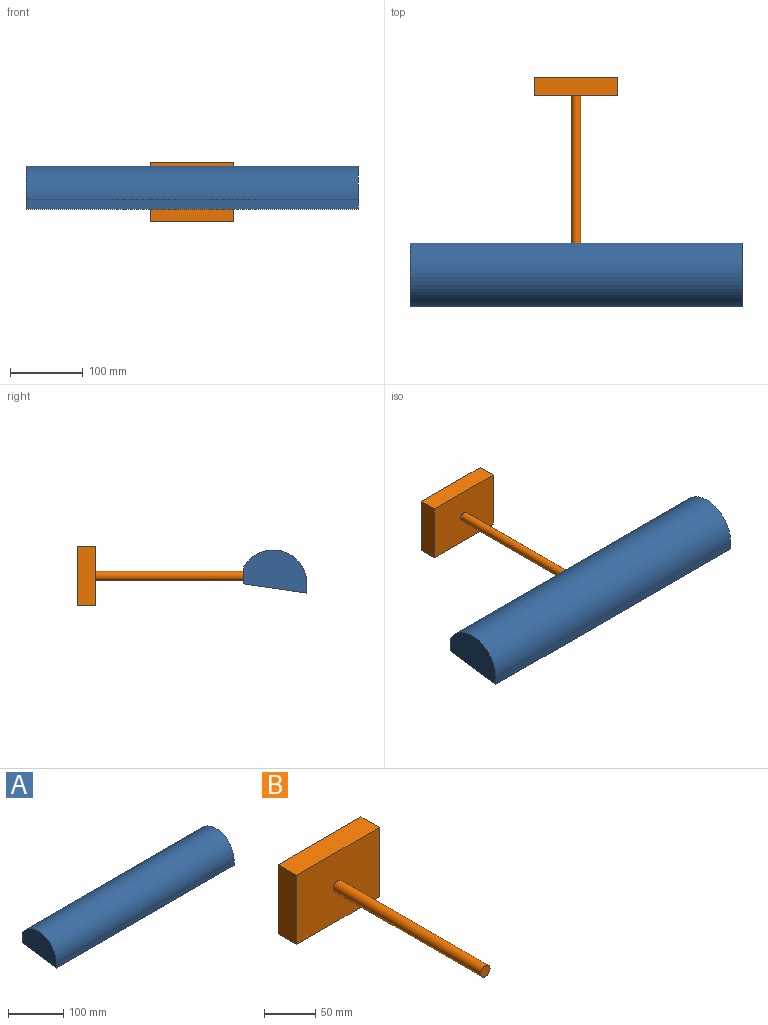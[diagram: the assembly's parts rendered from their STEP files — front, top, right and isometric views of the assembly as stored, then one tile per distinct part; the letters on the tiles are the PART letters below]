
ASSEMBLY  parts=2 mates=1
PART A: 6 faces, bbox 457.2x87.8x59.3 mm
  f0: plane 457.2x87.84mm, normal (0,0.14,-0.99), area 40577.9mm2, adj f1,f3,f4,f5
  f1: plane 457.2x21.59mm, normal (0,1,0), area 9871.5mm2, adj f0,f2,f4,f5
  f2: cylinder r=46.57mm len=457.2mm, axis (-1,0,0), area 56630.7mm2, adj f1,f3,f4,f5
  f3: plane 457.2x12.7mm, normal (0,-1,0), area 5806.4mm2, adj f0,f2,f4,f5
  f4: plane 87.84x59.27mm, normal (1,0,0), area 3887.7mm2, adj f0,f1,f2,f3
  f5: plane 87.84x59.27mm, normal (-1,0,0), area 3887.7mm2, adj f0,f1,f2,f3
PART B: 8 faces, bbox 114.3x228.6x82.6 mm
  f0: plane 82.55x25.4mm, normal (1,0,0), area 2096.8mm2, adj f1,f3,f4,f5
  f1: plane 114.3x25.4mm, normal (0,0,1), area 2903.2mm2, adj f0,f2,f4,f5
  f2: plane 82.55x25.4mm, normal (-1,0,0), area 2096.8mm2, adj f1,f3,f4,f5
  f3: plane 114.3x25.4mm, normal (0,0,-1), area 2903.2mm2, adj f0,f2,f4,f5
  f4: plane 114.3x82.55mm, normal (0,-1,0), area 9308.8mm2, adj f0,f1,f2,f3,f6
  f5: plane 114.3x82.55mm, normal (0,1,0), area 9435.5mm2, adj f0,f1,f2,f3
  f6: cylinder r=6.35mm len=203.2mm, axis (0,1,0), area 8107.3mm2, adj f4,f7
  f7: plane 12.7x12.7mm, normal (0,-1,0), area 126.7mm2, adj f6
PLACE A t=(-106.11,158.33,-90.09)mm
PLACE B t=(-106.11,158.11,-92.07)mm
MATE fastened B.f6 <-> A.f1  axis (0,-1,0) through (-106.11,-70.49,-92.07)mm
